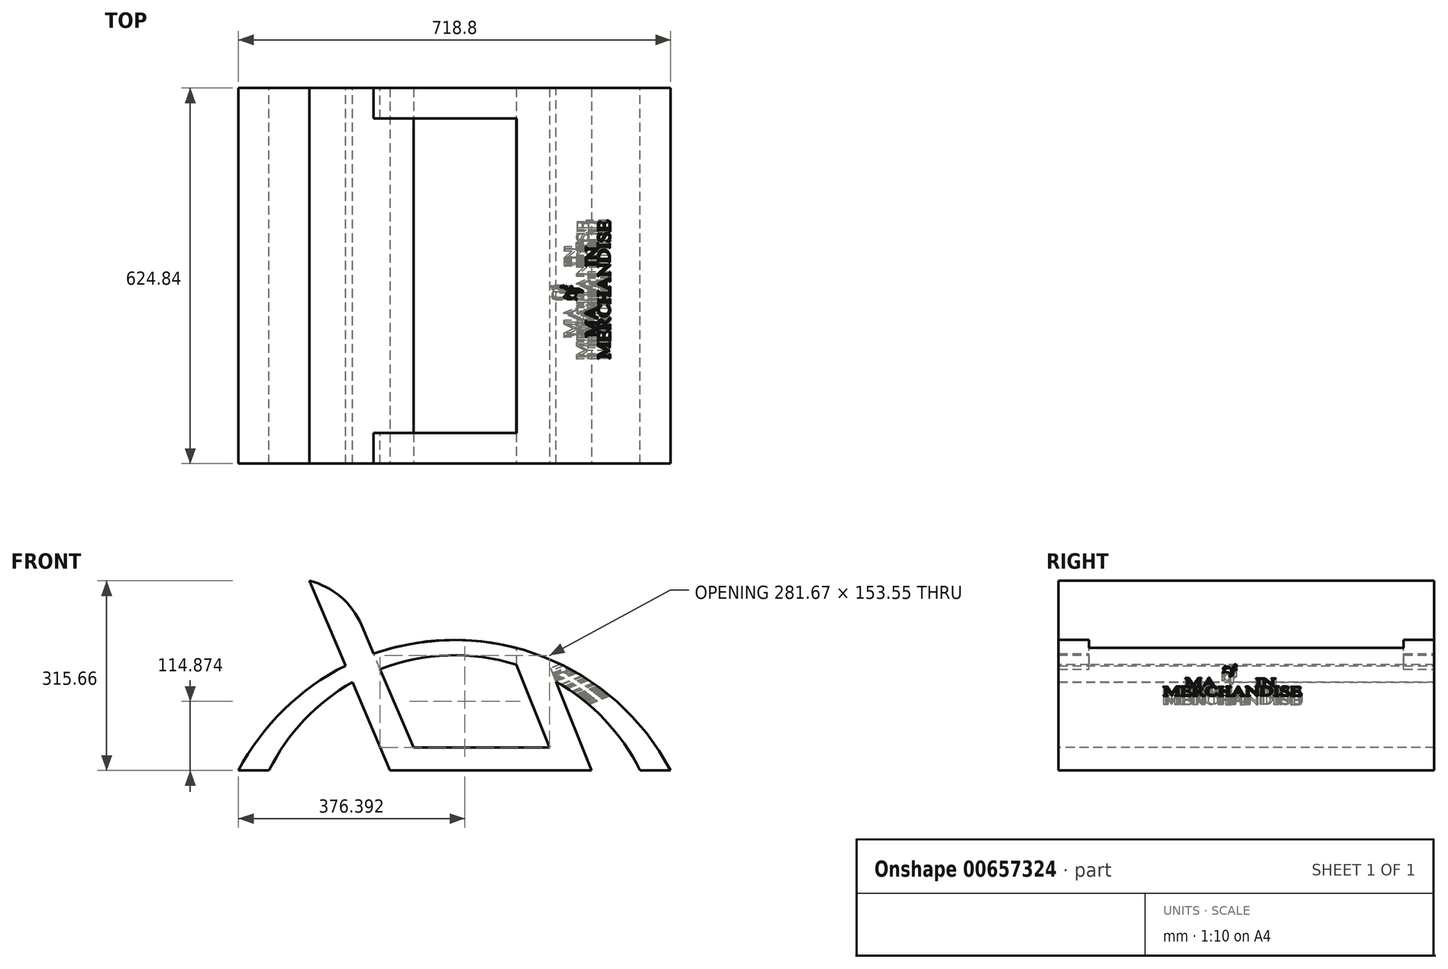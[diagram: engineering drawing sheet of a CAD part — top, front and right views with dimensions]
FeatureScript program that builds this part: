
annotation { "Feature Type Name" : "Feature", "Feature Type Description" : "" }
export const myFeature = defineFeature(function(context is Context, id is Id, definition is map)
    precondition{}
    {
        {
            var Q0;
            Q0=qCreatedBy(makeId("Front.planeOp"),FACE);
            var sketch = newSketch(context, id + "F0", { "sketchPlane" : qUnion([Q0])});
            skArc(sketch, "E0", {"start": v(359.4, -297.32) * mm, "mid": v(0, -80.1) * mm, "end": v(-359.4, -297.32) * mm});
            skArc(sketch, "E1", {"start": v(308.6, -297.32) * mm, "mid": v(0, -105.5) * mm, "end": v(-308.6, -297.32) * mm});
            skLineSegment(sketch, "E2", {"start": v(-359.4, -297.32) * mm, "end": v(-308.6, -297.32) * mm});
            skLineSegment(sketch, "E3", {"start": v(308.6, -297.32) * mm, "end": v(359.4, -297.32) * mm});
            skSolve(sketch);
        }
        {
            var Q0;
            Q0=qSketchRegion(id+"F0",true);
            extrude(context, id + "F1", {"entities" : qUnion([Q0]), "depth" : 624.84 * mm, "offsetDistance" : 25.4 * mm});
        }
        {
            var Q0;
            Q0=makeQuery(id+"F1.opExtrude","CAP_FACE",FACE,{"disambiguationData":[OSD([sQuery(id+"F0.wireOp",EDGE,"E0"),sQuery(id+"F0.wireOp",EDGE,"E1"),sQuery(id+"F0.wireOp",EDGE,"E2"),sQuery(id+"F0.wireOp",EDGE,"E3")])],"isStart":false});
            var sketch = newSketch(context, id + "F2", { "sketchPlane" : qUnion([Q0])});
            skLineSegment(sketch, "E4", {"start": v(-241.38, 18.34) * mm, "end": v(-107.4, -297.32) * mm});
            skLineSegment(sketch, "E5", {"start": v(-107.4, -297.32) * mm, "end": v(227.72, -297.32) * mm});
            skLineSegment(sketch, "E6", {"start": v(227.72, -297.32) * mm, "end": v(153.02, -110.04) * mm});
            skLineSegment(sketch, "E7", {"start": v(-68.38, -259.22) * mm, "end": v(157.83, -259.22) * mm});
            skLineSegment(sketch, "E8", {"start": v(157.83, -259.22) * mm, "end": v(102.78, -121.2) * mm});
            skLineSegment(sketch, "E9", {"start": v(102.78, -121.2) * mm, "end": v(153.02, -110.04) * mm});
            skLineSegment(sketch, "E10", {"start": v(-68.38, -259.22) * mm, "end": v(-154.8, -55.64) * mm});
            skArc(sketch, "E11", {"start": v(-154.8, -55.64) * mm, "mid": v(-189.38, -8.46) * mm, "end": v(-241.38, 18.34) * mm});
            skSolve(sketch);
        }
        {
            var Q0;
            Q0=qCreatedBy(makeId("Top.planeOp"),FACE);
            var sketch = newSketch(context, id + "F3", { "sketchPlane" : qUnion([Q0])});
            skLineSegment(sketch, "E12.bottom", {"start": v(-163.5, -50.8) * mm, "end": v(103.2, -50.8) * mm});
            skLineSegment(sketch, "E12.top", {"start": v(-163.5, -574.04) * mm, "end": v(103.2, -574.04) * mm});
            skLineSegment(sketch, "E12.left", {"start": v(-163.5, -50.8) * mm, "end": v(-163.5, -574.04) * mm});
            skLineSegment(sketch, "E12.right", {"start": v(103.2, -50.8) * mm, "end": v(103.2, -574.04) * mm});
            skSolve(sketch);
        }
        {
            var Q0;
            Q0=qSketchRegion(id+"F3",true);
            extrude(context, id + "F4", {"entities" : qUnion([Q0]), "operationType" : NewBodyOperationType.REMOVE, "oppositeDirection" : true, "depth" : 251.46 * mm, "offsetDistance" : 25.4 * mm});
        }
        {
            var Q0;
            Q0=qSketchRegion(id+"F2",true);
            extrude(context, id + "F5", {"entities" : qUnion([Q0]), "operationType" : NewBodyOperationType.ADD, "oppositeDirection" : true, "depth" : 624.84 * mm, "offsetDistance" : 25.4 * mm});
        }
        {
            var Q0;
            Q0=makeQuery(id+"F5.opExtrude","SWEPT_FACE",FACE,{"disambiguationData":[OSD([sQuery(id+"F2.wireOp",EDGE,"E6")])]});
            var sketch = newSketch(context, id + "F6", { "sketchPlane" : qUnion([Q0])});
            skFitSpline(sketch, "E13", {"points": [v(-335.35, -191.62) * mm, v(-335.44, -189.93) * mm, v(-335.7, -187.4) * mm, v(-334.92, -184.76) * mm, v(-333.7, -182.79) * mm, v(-332.39, -181.38) * mm, v(-332.12, -179.22) * mm, v(-331.95, -177.52) * mm, v(-331.08, -177.24) * mm, v(-329.94, -177.43) * mm, v(-329.77, -178.75) * mm, v(-329.42, -180.44) * mm, v(-328.2, -181.1) * mm, v(-328.54, -181.85) * mm, v(-329.42, -182.32) * mm, v(-329.77, -183.16) * mm, v(-329.77, -184.57) * mm, v(-329.85, -185.42) * mm, v(-330.99, -185.6) * mm, v(-331.95, -186.17) * mm, v(-333, -186.92) * mm, v(-333.6, -188.52) * mm, v(-333.87, -190.5) * mm, v(-333.87, -191.62) * mm, v(-332.82, -190.96) * mm, v(-331.08, -190.96) * mm, v(-329.42, -192.28) * mm, v(-329.6, -193.31) * mm, v(-331.95, -194.16) * mm, v(-333.26, -195.2) * mm, v(-333.87, -197.07) * mm, v(-333.96, -199.7) * mm], "startDerivative": vector(-0.27, 47.79) * mm, "endDerivative": vector(0.97, -64.68) * mm});
            skFitSpline(sketch, "E14", {"points": [v(-333.96, -199.7) * mm, v(-333.96, -201.04) * mm, v(-333.96, -202.6) * mm, v(-333.96, -203.72) * mm, v(-334.56, -205.07) * mm, v(-335.96, -207.75) * mm, v(-337.93, -209.6) * mm, v(-339.7, -209.76) * mm, v(-340.37, -208.92) * mm, v(-340.43, -208.42) * mm, v(-339.7, -208.48) * mm, v(-338.66, -207.8) * mm, v(-338.6, -206.58) * mm, v(-339.44, -205.51) * mm, v(-339.7, -203.56) * mm, v(-339.6, -202.5) * mm, v(-341.1, -201.2) * mm, v(-341.72, -201.15) * mm, v(-341.72, -200.15) * mm, v(-342.2, -199.2) * mm, v(-344.22, -199.25) * mm, v(-345.57, -199.09) * mm, v(-346.19, -198.2) * mm, v(-347.38, -196.8) * mm, v(-347.95, -196.9) * mm, v(-348.16, -198.14) * mm, v(-348.89, -198.97) * mm, v(-351.28, -200.15) * mm, v(-353.04, -198.92) * mm, v(-350.8, -198.7) * mm, v(-349.56, -196.8) * mm, v(-349.1, -194.5) * mm], "startDerivative": vector(0.31, -42.03) * mm, "endDerivative": vector(9.9, 54.9) * mm});
            skFitSpline(sketch, "E15", {"points": [v(-349.1, -194.5) * mm, v(-350.5, -193.44) * mm, v(-350.86, -192.66) * mm, v(-350.24, -192.1) * mm, v(-350.5, -191.43) * mm, v(-351.64, -190.42) * mm, v(-351.38, -189.98) * mm, v(-350.7, -189.42) * mm, v(-351.12, -188.41) * mm, v(-350.63, -187) * mm, v(-350.38, -186) * mm, v(-349.77, -185.53) * mm, v(-349.1, -184.2) * mm, v(-348.4, -183.34) * mm, v(-348.6, -182.14) * mm, v(-348.22, -181.81) * mm, v(-347.6, -181.61) * mm, v(-346.74, -182.28) * mm, v(-345.82, -183.47) * mm, v(-342.98, -184.54) * mm, v(-340.26, -186.4) * mm, v(-337.73, -189) * mm, v(-337.48, -189.92) * mm, v(-336.8, -190.32) * mm, v(-336.68, -190.65) * mm, v(-336.5, -191.38) * mm, v(-336.12, -192.25) * mm, v(-335.35, -191.62) * mm], "startDerivative": vector(-33.51, 22.16) * mm, "endDerivative": vector(25.24, 30.1) * mm});
            skFitSpline(sketch, "E16", {"points": [v(-349.7, -190.19) * mm, v(-349.03, -188.41) * mm, v(-347.67, -187.13) * mm, v(-347.42, -186.27) * mm, v(-346.99, -185.87) * mm, v(-346.37, -186) * mm, v(-346.06, -186.86) * mm, v(-345.75, -186) * mm, v(-344.77, -185.8) * mm, v(-343.16, -186.2) * mm, v(-341.3, -187.2) * mm, v(-340.14, -187.73) * mm, v(-339.02, -188.41) * mm, v(-338.65, -189.42) * mm, v(-338.35, -189.99) * mm, v(-338.53, -190.52) * mm, v(-339.95, -189.42) * mm, v(-341.62, -188.41) * mm, v(-343.16, -188.41) * mm, v(-344.7, -188.41) * mm, v(-345.63, -189.42) * mm, v(-346.74, -190.32) * mm, v(-347.54, -191.12) * mm, v(-348.22, -191.12) * mm, v(-349.7, -190.19) * mm]});
            skLineSegment(sketch, "E17", {"start": v(-442.75, -256.74) * mm, "end": v(-442.75, -255.25) * mm});
            skLineSegment(sketch, "E18", {"start": v(-442.75, -255.25) * mm, "end": v(-445.49, -255.25) * mm});
            skLineSegment(sketch, "E19", {"start": v(-445.49, -255.25) * mm, "end": v(-445.49, -239.64) * mm});
            skLineSegment(sketch, "E20", {"start": v(-445.49, -239.64) * mm, "end": v(-436.87, -256.58) * mm});
            skLineSegment(sketch, "E21", {"start": v(-436.87, -256.58) * mm, "end": v(-428.5, -238.13) * mm});
            skLineSegment(sketch, "E22", {"start": v(-428.5, -238.13) * mm, "end": v(-428.5, -255.16) * mm});
            skLineSegment(sketch, "E23", {"start": v(-428.5, -255.16) * mm, "end": v(-432.12, -255.16) * mm});
            skLineSegment(sketch, "E24", {"start": v(-432.12, -255.16) * mm, "end": v(-432.12, -256.33) * mm});
            skLineSegment(sketch, "E25", {"start": v(-432.12, -256.33) * mm, "end": v(-422.87, -256.33) * mm});
            skLineSegment(sketch, "E26", {"start": v(-422.87, -256.33) * mm, "end": v(-422.87, -255.25) * mm});
            skLineSegment(sketch, "E27", {"start": v(-422.87, -255.25) * mm, "end": v(-425.95, -255.25) * mm});
            skLineSegment(sketch, "E28", {"start": v(-425.95, -255.25) * mm, "end": v(-425.95, -235.85) * mm});
            skLineSegment(sketch, "E29", {"start": v(-425.95, -235.85) * mm, "end": v(-422.6, -235.85) * mm});
            skLineSegment(sketch, "E30", {"start": v(-422.6, -235.85) * mm, "end": v(-422.6, -234.76) * mm});
            skLineSegment(sketch, "E31", {"start": v(-422.6, -234.76) * mm, "end": v(-429.42, -234.76) * mm});
            skLineSegment(sketch, "E32", {"start": v(-429.42, -234.76) * mm, "end": v(-436.5, -250.52) * mm});
            skLineSegment(sketch, "E33", {"start": v(-436.5, -250.52) * mm, "end": v(-443.59, -234.98) * mm});
            skLineSegment(sketch, "E34", {"start": v(-443.59, -234.98) * mm, "end": v(-450.58, -234.98) * mm});
            skLineSegment(sketch, "E35", {"start": v(-450.58, -234.98) * mm, "end": v(-450.58, -235.98) * mm});
            skLineSegment(sketch, "E36", {"start": v(-450.58, -235.98) * mm, "end": v(-447.14, -235.98) * mm});
            skLineSegment(sketch, "E37", {"start": v(-447.14, -235.98) * mm, "end": v(-447.14, -255.15) * mm});
            skLineSegment(sketch, "E38", {"start": v(-447.14, -255.15) * mm, "end": v(-450.16, -255.15) * mm});
            skLineSegment(sketch, "E39", {"start": v(-450.16, -255.15) * mm, "end": v(-450.22, -256.74) * mm});
            skLineSegment(sketch, "E40", {"start": v(-421.53, -234.76) * mm, "end": v(-421.53, -235.85) * mm});
            skLineSegment(sketch, "E41", {"start": v(-421.53, -235.85) * mm, "end": v(-418.8, -235.85) * mm});
            skLineSegment(sketch, "E42", {"start": v(-418.8, -235.85) * mm, "end": v(-418.8, -255.15) * mm});
            skLineSegment(sketch, "E43", {"start": v(-418.8, -255.15) * mm, "end": v(-421.79, -255.15) * mm});
            skLineSegment(sketch, "E44", {"start": v(-421.79, -255.15) * mm, "end": v(-421.79, -256.69) * mm});
            skLineSegment(sketch, "E45", {"start": v(-421.79, -256.69) * mm, "end": v(-405.11, -256.69) * mm});
            skLineSegment(sketch, "E46", {"start": v(-405.11, -256.69) * mm, "end": v(-402.76, -251.15) * mm});
            skLineSegment(sketch, "E47", {"start": v(-402.76, -251.15) * mm, "end": v(-404.21, -250.53) * mm});
            skLineSegment(sketch, "E48", {"start": v(-404.21, -250.53) * mm, "end": v(-406.27, -255.4) * mm});
            skLineSegment(sketch, "E49", {"start": v(-406.27, -255.4) * mm, "end": v(-415.53, -255.4) * mm});
            skLineSegment(sketch, "E50", {"start": v(-415.53, -255.4) * mm, "end": v(-415.53, -246.5) * mm});
            skLineSegment(sketch, "E51", {"start": v(-415.53, -246.5) * mm, "end": v(-408.78, -246.5) * mm});
            skArc(sketch, "E52", {"start": v(-407.98, -249.08) * mm, "mid": v(-408.19, -247.74) * mm, "end": v(-408.78, -246.5) * mm});
            skArc(sketch, "E53", {"start": v(-408.78, -244.41) * mm, "mid": v(-408.02, -243.45) * mm, "end": v(-407.67, -242.28) * mm});
            skLineSegment(sketch, "E54", {"start": v(-407.67, -242.28) * mm, "end": v(-407.17, -242.28) * mm});
            skLineSegment(sketch, "E55", {"start": v(-407.17, -242.28) * mm, "end": v(-407.17, -249.05) * mm});
            skLineSegment(sketch, "E56", {"start": v(-407.17, -249.05) * mm, "end": v(-407.98, -249.08) * mm});
            skLineSegment(sketch, "E57", {"start": v(-415.53, -244.52) * mm, "end": v(-408.78, -244.41) * mm});
            skLineSegment(sketch, "E58", {"start": v(-415.53, -244.52) * mm, "end": v(-415.66, -236.48) * mm});
            skLineSegment(sketch, "E59", {"start": v(-415.66, -236.48) * mm, "end": v(-407.47, -236.48) * mm});
            skArc(sketch, "E60", {"start": v(-406.33, -239.98) * mm, "mid": v(-406.3, -238.04) * mm, "end": v(-407.47, -236.48) * mm});
            skLineSegment(sketch, "E61", {"start": v(-406.33, -239.98) * mm, "end": v(-405.19, -239.98) * mm});
            skLineSegment(sketch, "E62", {"start": v(-405.19, -239.98) * mm, "end": v(-405.19, -234.83) * mm});
            skLineSegment(sketch, "E63", {"start": v(-405.19, -234.83) * mm, "end": v(-421.53, -234.76) * mm});
            skLineSegment(sketch, "E64", {"start": v(-238.9, -235.08) * mm, "end": v(-238.9, -236.18) * mm});
            skLineSegment(sketch, "E65", {"start": v(-238.9, -236.18) * mm, "end": v(-236.17, -236.18) * mm});
            skLineSegment(sketch, "E66", {"start": v(-236.17, -236.18) * mm, "end": v(-236.19, -255.48) * mm});
            skLineSegment(sketch, "E67", {"start": v(-236.19, -255.48) * mm, "end": v(-239.16, -255.48) * mm});
            skLineSegment(sketch, "E68", {"start": v(-239.16, -255.48) * mm, "end": v(-239.16, -257.01) * mm});
            skLineSegment(sketch, "E69", {"start": v(-239.16, -257.01) * mm, "end": v(-222.2, -257.02) * mm});
            skLineSegment(sketch, "E70", {"start": v(-222.2, -257.02) * mm, "end": v(-220.14, -251.49) * mm});
            skLineSegment(sketch, "E71", {"start": v(-220.14, -251.49) * mm, "end": v(-221.83, -250.85) * mm});
            skLineSegment(sketch, "E72", {"start": v(-221.83, -250.85) * mm, "end": v(-223.1, -254.27) * mm});
            skArc(sketch, "E73", {"start": v(-224.85, -255.85) * mm, "mid": v(-223.79, -255.27) * mm, "end": v(-223.1, -254.27) * mm});
            skLineSegment(sketch, "E74", {"start": v(-224.85, -255.85) * mm, "end": v(-232.91, -255.84) * mm});
            skLineSegment(sketch, "E75", {"start": v(-232.91, -255.84) * mm, "end": v(-232.9, -246.84) * mm});
            skLineSegment(sketch, "E76", {"start": v(-232.9, -246.84) * mm, "end": v(-226.15, -246.84) * mm});
            skArc(sketch, "E77", {"start": v(-225.35, -249.42) * mm, "mid": v(-225.56, -248.07) * mm, "end": v(-226.15, -246.84) * mm});
            skArc(sketch, "E78", {"start": v(-226.15, -244.75) * mm, "mid": v(-225.4, -243.79) * mm, "end": v(-225.04, -242.62) * mm});
            skLineSegment(sketch, "E79", {"start": v(-225.04, -242.62) * mm, "end": v(-224.54, -242.62) * mm});
            skLineSegment(sketch, "E80", {"start": v(-224.54, -242.62) * mm, "end": v(-224.54, -249.38) * mm});
            skLineSegment(sketch, "E81", {"start": v(-224.54, -249.38) * mm, "end": v(-225.35, -249.42) * mm});
            skLineSegment(sketch, "E82", {"start": v(-232.9, -244.85) * mm, "end": v(-226.15, -244.75) * mm});
            skLineSegment(sketch, "E83", {"start": v(-232.9, -244.85) * mm, "end": v(-233.02, -236.8) * mm});
            skLineSegment(sketch, "E84", {"start": v(-233.02, -236.8) * mm, "end": v(-224.84, -236.81) * mm});
            skArc(sketch, "E85", {"start": v(-223.7, -240.32) * mm, "mid": v(-223.67, -238.37) * mm, "end": v(-224.84, -236.81) * mm});
            skLineSegment(sketch, "E86", {"start": v(-223.7, -240.32) * mm, "end": v(-222.56, -240.32) * mm});
            skLineSegment(sketch, "E87", {"start": v(-222.56, -240.32) * mm, "end": v(-222.55, -235.16) * mm});
            skLineSegment(sketch, "E88", {"start": v(-222.55, -235.16) * mm, "end": v(-238.9, -235.08) * mm});
            skLineSegment(sketch, "E89.0", {"start": v(-232.9, -246.84) * mm, "end": v(-232.9, -244.85) * mm, "construction": true});
            skLineSegment(sketch, "E90.0", {"start": v(-226.15, -246.84) * mm, "end": v(-226.15, -244.75) * mm, "construction": true});
            skLineSegment(sketch, "E91", {"start": v(-399.46, -255.4) * mm, "end": v(-399.46, -236.97) * mm});
            skLineSegment(sketch, "E92", {"start": v(-399.46, -236.97) * mm, "end": v(-402.49, -235.68) * mm});
            skLineSegment(sketch, "E93", {"start": v(-402.49, -235.68) * mm, "end": v(-402.5, -234.44) * mm});
            skLineSegment(sketch, "E94", {"start": v(-402.5, -234.44) * mm, "end": v(-391.04, -234.44) * mm});
            skArc(sketch, "E95", {"start": v(-391.04, -245.74) * mm, "mid": v(-385.39, -240.09) * mm, "end": v(-391.04, -234.44) * mm});
            skArc(sketch, "E96", {"start": v(-395.75, -244.84) * mm, "mid": v(-389.61, -240.3) * mm, "end": v(-396.09, -236.25) * mm});
            skLineSegment(sketch, "E97", {"start": v(-396.09, -236.25) * mm, "end": v(-395.75, -244.84) * mm});
            skLineSegment(sketch, "E98", {"start": v(-395.75, -246.71) * mm, "end": v(-395.75, -255.4) * mm});
            skLineSegment(sketch, "E99", {"start": v(-395.75, -255.4) * mm, "end": v(-392.97, -255.4) * mm});
            skLineSegment(sketch, "E100", {"start": v(-392.97, -255.4) * mm, "end": v(-392.97, -256.66) * mm});
            skLineSegment(sketch, "E101", {"start": v(-392.97, -256.66) * mm, "end": v(-402.31, -256.66) * mm});
            skLineSegment(sketch, "E102", {"start": v(-402.31, -256.66) * mm, "end": v(-402.31, -255.4) * mm});
            skLineSegment(sketch, "E103", {"start": v(-402.31, -255.4) * mm, "end": v(-399.46, -255.4) * mm});
            skLineSegment(sketch, "E104", {"start": v(-395.75, -246.71) * mm, "end": v(-393.76, -246.71) * mm});
            skLineSegment(sketch, "E105", {"start": v(-393.76, -246.71) * mm, "end": v(-386.57, -256.7) * mm});
            skLineSegment(sketch, "E106", {"start": v(-386.57, -256.7) * mm, "end": v(-381.36, -256.7) * mm});
            skLineSegment(sketch, "E107", {"start": v(-381.36, -256.7) * mm, "end": v(-381.36, -255.4) * mm});
            skLineSegment(sketch, "E108", {"start": v(-381.36, -255.4) * mm, "end": v(-384.07, -255.4) * mm});
            skLineSegment(sketch, "E109", {"start": v(-384.07, -255.4) * mm, "end": v(-391.04, -245.74) * mm});
            skLineSegment(sketch, "E110", {"start": v(-362.13, -234.46) * mm, "end": v(-362.13, -241.27) * mm});
            skLineSegment(sketch, "E111", {"start": v(-363.87, -236.24) * mm, "end": v(-362.13, -234.46) * mm});
            skArc(sketch, "E112", {"start": v(-363.87, -236.24) * mm, "mid": v(-380.25, -244.3) * mm, "end": v(-366.7, -256.56) * mm});
            skFitSpline(sketch, "E113", {"points": [v(-362.13, -241.27) * mm, v(-364.55, -237.77) * mm, v(-368.44, -236.32) * mm, v(-372.72, -237.44) * mm, v(-375.26, -241.59) * mm], "startDerivative": vector(-8.42, 15.94) * mm, "endDerivative": vector(-7.7, -18.3) * mm});
            skFitSpline(sketch, "E114", {"points": [v(-375.26, -241.59) * mm, v(-375.68, -249.47) * mm, v(-373.4, -253.08) * mm, v(-370.42, -254.51) * mm, v(-367.3, -254.85) * mm, v(-364.88, -253.73) * mm, v(-362.13, -250.86) * mm, v(-361.3, -250.74) * mm, v(-361.06, -251.65) * mm, v(-362.13, -253.6) * mm, v(-363.84, -255.43) * mm, v(-366.7, -256.56) * mm], "startDerivative": vector(-9.26, -57.49) * mm, "endDerivative": vector(-33.48, -9.75) * mm});
            skArc(sketch, "E115", {"start": v(-284.23, -254.17) * mm, "mid": v(-272.32, -245.7) * mm, "end": v(-284.2, -237.18) * mm});
            skArc(sketch, "E116", {"start": v(-278.73, -255.89) * mm, "mid": v(-268.91, -245.3) * mm, "end": v(-278.5, -234.52) * mm});
            skLineSegment(sketch, "E117", {"start": v(-278.73, -255.89) * mm, "end": v(-289.78, -255.89) * mm});
            skLineSegment(sketch, "E118", {"start": v(-289.78, -255.89) * mm, "end": v(-289.78, -254.4) * mm});
            skLineSegment(sketch, "E119", {"start": v(-289.78, -254.4) * mm, "end": v(-287.8, -254.4) * mm});
            skLineSegment(sketch, "E120", {"start": v(-287.8, -254.4) * mm, "end": v(-287.3, -235.76) * mm});
            skLineSegment(sketch, "E121", {"start": v(-287.3, -235.76) * mm, "end": v(-290.05, -235.7) * mm});
            skLineSegment(sketch, "E122", {"start": v(-290.05, -235.7) * mm, "end": v(-290.05, -234.57) * mm});
            skLineSegment(sketch, "E123", {"start": v(-290.05, -234.57) * mm, "end": v(-278.5, -234.52) * mm});
            skLineSegment(sketch, "E124", {"start": v(-353.22, -244.38) * mm, "end": v(-343.8, -244.38) * mm});
            skLineSegment(sketch, "E125", {"start": v(-353.42, -254.95) * mm, "end": v(-353.42, -246.74) * mm});
            skLineSegment(sketch, "E126", {"start": v(-353.42, -246.74) * mm, "end": v(-343.93, -246.74) * mm});
            skFitSpline(sketch, "E127", {"points": [v(-353.42, -254.95) * mm, v(-353.15, -255.5) * mm, v(-352.52, -255.63) * mm], "startDerivative": vector(0.37, -1.35) * mm, "endDerivative": vector(1.42, 0.17) * mm});
            skLineSegment(sketch, "E128", {"start": v(-352.52, -255.63) * mm, "end": v(-350.68, -255.63) * mm});
            skLineSegment(sketch, "E129", {"start": v(-350.68, -255.63) * mm, "end": v(-350.68, -256.68) * mm});
            skLineSegment(sketch, "E130", {"start": v(-350.68, -256.68) * mm, "end": v(-358.19, -256.68) * mm});
            skLineSegment(sketch, "E131", {"start": v(-358.19, -256.68) * mm, "end": v(-359.36, -256.68) * mm});
            skLineSegment(sketch, "E132", {"start": v(-359.36, -256.68) * mm, "end": v(-359.36, -255.63) * mm});
            skLineSegment(sketch, "E133", {"start": v(-359.36, -255.63) * mm, "end": v(-357.47, -255.63) * mm});
            skLineSegment(sketch, "E134", {"start": v(-356.6, -255.3) * mm, "end": v(-356.6, -237.36) * mm});
            skFitSpline(sketch, "E135", {"points": [v(-356.6, -237.36) * mm, v(-356.9, -236.25) * mm, v(-358.24, -236.05) * mm], "startDerivative": vector(-0.68, 2.41) * mm, "endDerivative": vector(-2.6, 0.22) * mm});
            skLineSegment(sketch, "E136", {"start": v(-358.24, -236.05) * mm, "end": v(-359.43, -236.05) * mm});
            skLineSegment(sketch, "E137", {"start": v(-359.43, -236.05) * mm, "end": v(-359.43, -235.16) * mm});
            skLineSegment(sketch, "E138", {"start": v(-359.43, -235.16) * mm, "end": v(-350.57, -235.16) * mm});
            skLineSegment(sketch, "E139", {"start": v(-350.57, -235.16) * mm, "end": v(-350.57, -236.05) * mm});
            skLineSegment(sketch, "E140", {"start": v(-353.22, -244.38) * mm, "end": v(-353.22, -237.04) * mm});
            skFitSpline(sketch, "E141", {"points": [v(-353.22, -237.04) * mm, v(-353.1, -236.33) * mm, v(-352.32, -236.12) * mm, v(-350.57, -236.05) * mm], "startDerivative": vector(-0.04, 3) * mm, "endDerivative": vector(4.3, 0.15) * mm});
            skFitSpline(sketch, "E142", {"points": [v(-350.55, -236.03) * mm, v(-350.57, -236.02) * mm], "startDerivative": vector(-0.01, 0.01) * mm, "endDerivative": vector(-0.01, 0.01) * mm});
            skLineSegment(sketch, "E143", {"start": v(-284.23, -254.17) * mm, "end": v(-284.2, -237.18) * mm});
            skLineSegment(sketch, "E144", {"start": v(-267.04, -234.4) * mm, "end": v(-257.34, -234.4) * mm});
            skLineSegment(sketch, "E145", {"start": v(-257.34, -234.4) * mm, "end": v(-257.34, -235.74) * mm});
            skLineSegment(sketch, "E146", {"start": v(-257.34, -235.74) * mm, "end": v(-259.85, -235.74) * mm});
            skFitSpline(sketch, "E147", {"points": [v(-261.19, -237.54) * mm, v(-261.02, -236.68) * mm, v(-260.49, -236.04) * mm, v(-259.85, -235.74) * mm], "startDerivative": vector(0.2, 2.55) * mm, "endDerivative": vector(2.11, 0.73) * mm});
            skLineSegment(sketch, "E148", {"start": v(-261.19, -237.54) * mm, "end": v(-261.19, -253.88) * mm});
            skFitSpline(sketch, "E149", {"points": [v(-261.19, -253.88) * mm, v(-260.88, -254.79) * mm, v(-260.52, -255.24) * mm, v(-259.84, -255.26) * mm], "startDerivative": vector(0.77, -2.51) * mm, "endDerivative": vector(2.36, 0.38) * mm});
            skLineSegment(sketch, "E150", {"start": v(-259.84, -255.26) * mm, "end": v(-258.16, -255.26) * mm});
            skLineSegment(sketch, "E151", {"start": v(-258.16, -255.26) * mm, "end": v(-258.16, -256.42) * mm});
            skLineSegment(sketch, "E152", {"start": v(-258.16, -256.42) * mm, "end": v(-266.64, -256.42) * mm});
            skLineSegment(sketch, "E153", {"start": v(-266.64, -256.42) * mm, "end": v(-266.64, -255.24) * mm});
            skFitSpline(sketch, "E154", {"points": [v(-266.64, -255.24) * mm, v(-264.58, -255.24) * mm, v(-263.91, -253.62) * mm], "startDerivative": vector(2.9, -0.56) * mm, "endDerivative": vector(0.76, 2.78) * mm});
            skLineSegment(sketch, "E155", {"start": v(-267.04, -234.4) * mm, "end": v(-267.04, -236.03) * mm});
            skFitSpline(sketch, "E156", {"points": [v(-267.04, -236.03) * mm, v(-264.62, -236.03) * mm, v(-263.91, -237.31) * mm], "startDerivative": vector(4.2, 0.09) * mm, "endDerivative": vector(-0.03, -6.33) * mm});
            skLineSegment(sketch, "E157", {"start": v(-263.91, -237.31) * mm, "end": v(-263.91, -253.62) * mm});
            skLineSegment(sketch, "E158", {"start": v(-329.38, -247.56) * mm, "end": v(-326.39, -239.8) * mm});
            skLineSegment(sketch, "E159", {"start": v(-326.39, -239.8) * mm, "end": v(-323.06, -247.74) * mm});
            skLineSegment(sketch, "E160", {"start": v(-323.06, -247.74) * mm, "end": v(-329.38, -247.56) * mm});
            skLineSegment(sketch, "E161", {"start": v(-332.84, -255.44) * mm, "end": v(-330.66, -249.6) * mm});
            skLineSegment(sketch, "E162", {"start": v(-330.66, -249.6) * mm, "end": v(-322.33, -249.6) * mm});
            skLineSegment(sketch, "E163", {"start": v(-322.33, -249.6) * mm, "end": v(-320.16, -255.43) * mm});
            skLineSegment(sketch, "E164", {"start": v(-336.48, -256.64) * mm, "end": v(-330.32, -256.64) * mm});
            skLineSegment(sketch, "E165", {"start": v(-322.7, -256.82) * mm, "end": v(-314.7, -256.82) * mm});
            skLineSegment(sketch, "E166", {"start": v(-314.7, -256.82) * mm, "end": v(-314.7, -255.43) * mm});
            skLineSegment(sketch, "E167", {"start": v(-335.07, -255.43) * mm, "end": v(-326.63, -234.81) * mm});
            skLineSegment(sketch, "E168", {"start": v(-326.63, -234.81) * mm, "end": v(-325.16, -234.81) * mm});
            skLineSegment(sketch, "E169", {"start": v(-325.16, -234.81) * mm, "end": v(-316.57, -255.43) * mm});
            skLineSegment(sketch, "E170", {"start": v(-316.57, -255.43) * mm, "end": v(-314.7, -255.43) * mm});
            skLineSegment(sketch, "E171", {"start": v(-336.48, -255.43) * mm, "end": v(-335.07, -255.43) * mm});
            skLineSegment(sketch, "E172", {"start": v(-336.48, -256.64) * mm, "end": v(-336.48, -255.43) * mm});
            skLineSegment(sketch, "E173", {"start": v(-332.84, -255.44) * mm, "end": v(-330.32, -255.44) * mm});
            skLineSegment(sketch, "E174", {"start": v(-330.32, -255.44) * mm, "end": v(-330.32, -256.64) * mm});
            skLineSegment(sketch, "E175", {"start": v(-322.7, -255.43) * mm, "end": v(-320.16, -255.43) * mm});
            skLineSegment(sketch, "E176", {"start": v(-322.7, -255.43) * mm, "end": v(-322.7, -256.82) * mm});
            skLineSegment(sketch, "E177", {"start": v(-450.22, -256.74) * mm, "end": v(-442.75, -256.74) * mm});
            skLineSegment(sketch, "E178", {"start": v(-298.15, -234.57) * mm, "end": v(-291.53, -234.57) * mm});
            skLineSegment(sketch, "E179", {"start": v(-291.53, -234.57) * mm, "end": v(-291.53, -235.88) * mm});
            skLineSegment(sketch, "E180", {"start": v(-291.53, -235.88) * mm, "end": v(-293.87, -235.88) * mm});
            skLineSegment(sketch, "E181", {"start": v(-293.87, -235.88) * mm, "end": v(-293.87, -256.81) * mm});
            skLineSegment(sketch, "E182", {"start": v(-293.87, -256.81) * mm, "end": v(-295.3, -256.81) * mm});
            skLineSegment(sketch, "E183", {"start": v(-295.3, -256.81) * mm, "end": v(-308.9, -239.62) * mm});
            skLineSegment(sketch, "E184", {"start": v(-308.9, -239.62) * mm, "end": v(-308.9, -255.59) * mm});
            skLineSegment(sketch, "E185", {"start": v(-308.9, -255.59) * mm, "end": v(-306.2, -255.59) * mm});
            skLineSegment(sketch, "E186", {"start": v(-306.2, -255.59) * mm, "end": v(-306.2, -256.65) * mm});
            skLineSegment(sketch, "E187", {"start": v(-306.2, -256.65) * mm, "end": v(-313.25, -256.65) * mm});
            skLineSegment(sketch, "E188", {"start": v(-313.25, -256.65) * mm, "end": v(-313.25, -255.55) * mm});
            skLineSegment(sketch, "E189", {"start": v(-313.25, -255.55) * mm, "end": v(-310.58, -255.55) * mm});
            skLineSegment(sketch, "E190", {"start": v(-310.58, -255.55) * mm, "end": v(-310.58, -236.8) * mm});
            skLineSegment(sketch, "E191", {"start": v(-310.58, -236.8) * mm, "end": v(-310.95, -236.37) * mm});
            skLineSegment(sketch, "E192", {"start": v(-310.95, -236.37) * mm, "end": v(-313.78, -236.37) * mm});
            skLineSegment(sketch, "E193", {"start": v(-313.78, -236.37) * mm, "end": v(-313.78, -234.73) * mm});
            skLineSegment(sketch, "E194", {"start": v(-313.78, -234.73) * mm, "end": v(-308.9, -234.73) * mm});
            skLineSegment(sketch, "E195", {"start": v(-308.9, -234.73) * mm, "end": v(-295.75, -250.35) * mm});
            skLineSegment(sketch, "E196", {"start": v(-295.75, -250.35) * mm, "end": v(-295.75, -235.76) * mm});
            skLineSegment(sketch, "E197", {"start": v(-295.75, -235.76) * mm, "end": v(-298.15, -235.76) * mm});
            skLineSegment(sketch, "E198", {"start": v(-298.15, -235.76) * mm, "end": v(-298.15, -234.57) * mm});
            skLineSegment(sketch, "E199", {"start": v(-242.58, -242.07) * mm, "end": v(-242.58, -234.65) * mm});
            skLineSegment(sketch, "E200", {"start": v(-242.58, -234.65) * mm, "end": v(-243.18, -234.65) * mm});
            skLineSegment(sketch, "E201", {"start": v(-242.58, -242.07) * mm, "end": v(-243.38, -242.07) * mm});
            skFitSpline(sketch, "E202", {"points": [v(-243.18, -234.65) * mm, v(-243.18, -235.64) * mm, v(-244.29, -235.67) * mm, v(-245.9, -234.65) * mm, v(-250.62, -234.65) * mm, v(-253.65, -236.3) * mm, v(-254.9, -240.06) * mm, v(-254.62, -242.7) * mm, v(-252.08, -245.1) * mm, v(-245, -249.34) * mm, v(-243.9, -252.12) * mm, v(-245.1, -254.46) * mm, v(-248.44, -255.2) * mm, v(-251.34, -254.31) * mm, v(-253.58, -252.04) * mm, v(-253.95, -249.5) * mm], "startDerivative": vector(8.48, -32.81) * mm, "endDerivative": vector(0.27, 42.67) * mm});
            skFitSpline(sketch, "E203", {"points": [v(-243.38, -242.07) * mm, v(-243.94, -238.78) * mm, v(-246.46, -237.04) * mm, v(-250.42, -236.9) * mm, v(-252.27, -237.92) * mm, v(-252.2, -240.31) * mm, v(-250.75, -242.07) * mm, v(-246.4, -244.5) * mm, v(-241.75, -248.19) * mm, v(-241.33, -253.38) * mm, v(-245, -256.66) * mm, v(-250.1, -256.98) * mm, v(-252.28, -255.8) * mm, v(-253.3, -255.32) * mm, v(-253.95, -255.56) * mm, v(-254.03, -256.53) * mm], "startDerivative": vector(-1.08, 51.46) * mm, "endDerivative": vector(3.1, -29.81) * mm});
            skLineSegment(sketch, "E204", {"start": v(-254.03, -256.53) * mm, "end": v(-254.03, -257.05) * mm});
            skLineSegment(sketch, "E205", {"start": v(-254.03, -257.05) * mm, "end": v(-255.15, -257.05) * mm});
            skLineSegment(sketch, "E206", {"start": v(-255.15, -257.05) * mm, "end": v(-255.15, -249.44) * mm});
            skLineSegment(sketch, "E207", {"start": v(-255.15, -249.44) * mm, "end": v(-253.95, -249.5) * mm});
            skFitSpline(sketch, "E208", {"points": [v(-357.47, -255.63) * mm, v(-357.21, -255.63) * mm, v(-356.91, -255.56) * mm, v(-356.73, -255.48) * mm, v(-356.6, -255.3) * mm], "startDerivative": vector(0.97, -0.06) * mm, "endDerivative": vector(0.5, 0.87) * mm});
            skLineSegment(sketch, "E209", {"start": v(-343.93, -246.74) * mm, "end": v(-343.93, -254.57) * mm});
            skLineSegment(sketch, "E210", {"start": v(-340.93, -254.57) * mm, "end": v(-340.93, -237.37) * mm});
            skLineSegment(sketch, "E211", {"start": v(-343.66, -237.24) * mm, "end": v(-343.8, -244.38) * mm});
            skLineSegment(sketch, "E212", {"start": v(-347.04, -255.43) * mm, "end": v(-347.04, -256.9) * mm});
            skLineSegment(sketch, "E213", {"start": v(-347.04, -256.9) * mm, "end": v(-337.23, -256.9) * mm});
            skLineSegment(sketch, "E214", {"start": v(-337.23, -256.9) * mm, "end": v(-337.23, -255.76) * mm});
            skLineSegment(sketch, "E215", {"start": v(-337.23, -255.76) * mm, "end": v(-339.47, -255.76) * mm});
            skFitSpline(sketch, "E216", {"points": [v(-347.04, -255.43) * mm, v(-345.67, -255.43) * mm, v(-344.3, -255.43) * mm, v(-343.93, -254.57) * mm], "startDerivative": vector(4.85, -0.05) * mm, "endDerivative": vector(0.33, 4.53) * mm});
            skFitSpline(sketch, "E217", {"points": [v(-340.93, -254.57) * mm, v(-340.93, -255.43) * mm, v(-339.47, -255.76) * mm], "startDerivative": vector(0.14, -1.71) * mm, "endDerivative": vector(4.5, 0.27) * mm});
            skLineSegment(sketch, "E218", {"start": v(-347.16, -235.87) * mm, "end": v(-347.16, -234.74) * mm});
            skLineSegment(sketch, "E219", {"start": v(-347.16, -234.74) * mm, "end": v(-337.15, -234.74) * mm});
            skLineSegment(sketch, "E220", {"start": v(-337.15, -234.74) * mm, "end": v(-337.15, -235.92) * mm});
            skLineSegment(sketch, "E221", {"start": v(-337.15, -235.92) * mm, "end": v(-339.38, -235.92) * mm});
            skLineSegment(sketch, "E222", {"start": v(-347.16, -235.87) * mm, "end": v(-344.48, -235.87) * mm});
            skFitSpline(sketch, "E223", {"points": [v(-344.48, -235.87) * mm, v(-343.66, -237.24) * mm], "startDerivative": vector(2.58, -0.16) * mm, "endDerivative": vector(-0.12, -2.08) * mm});
            skFitSpline(sketch, "E224", {"points": [v(-340.93, -237.37) * mm, v(-339.38, -235.92) * mm], "startDerivative": vector(-0.12, 2.88) * mm, "endDerivative": vector(4.42, -0.05) * mm});
            skLineSegment(sketch, "E225", {"start": v(-409.6, -233.52) * mm, "end": v(-409.6, -218.43) * mm});
            skLineSegment(sketch, "E226", {"start": v(-392.87, -218.65) * mm, "end": v(-392.87, -233.52) * mm});
            skLineSegment(sketch, "E227", {"start": v(-389.56, -233.59) * mm, "end": v(-389.56, -215.24) * mm});
            skLineSegment(sketch, "E228", {"start": v(-389.56, -215.24) * mm, "end": v(-386.67, -215.24) * mm});
            skLineSegment(sketch, "E229", {"start": v(-386.67, -215.24) * mm, "end": v(-386.67, -214.13) * mm});
            skLineSegment(sketch, "E230", {"start": v(-386.67, -214.13) * mm, "end": v(-392.81, -214.13) * mm});
            skLineSegment(sketch, "E231", {"start": v(-392.81, -214.13) * mm, "end": v(-400.4, -229.96) * mm});
            skLineSegment(sketch, "E232", {"start": v(-400.4, -229.96) * mm, "end": v(-407.75, -214.13) * mm});
            skLineSegment(sketch, "E233", {"start": v(-407.75, -214.13) * mm, "end": v(-414.54, -214.13) * mm});
            skLineSegment(sketch, "E234", {"start": v(-414.54, -214.13) * mm, "end": v(-414.54, -215.59) * mm});
            skLineSegment(sketch, "E235", {"start": v(-414.54, -215.59) * mm, "end": v(-411.24, -215.59) * mm});
            skLineSegment(sketch, "E236", {"start": v(-411.24, -215.59) * mm, "end": v(-411.24, -233.52) * mm});
            skLineSegment(sketch, "E237", {"start": v(-411.24, -233.52) * mm, "end": v(-409.6, -233.52) * mm});
            skLineSegment(sketch, "E238", {"start": v(-409.6, -218.43) * mm, "end": v(-402.5, -233.52) * mm});
            skLineSegment(sketch, "E239", {"start": v(-402.5, -233.52) * mm, "end": v(-399.75, -233.52) * mm});
            skLineSegment(sketch, "E240", {"start": v(-399.75, -233.52) * mm, "end": v(-392.87, -218.65) * mm});
            skLineSegment(sketch, "E241", {"start": v(-378.17, -226.06) * mm, "end": v(-375.17, -218.3) * mm});
            skLineSegment(sketch, "E242", {"start": v(-375.17, -218.3) * mm, "end": v(-371.85, -226.24) * mm});
            skLineSegment(sketch, "E243", {"start": v(-371.85, -226.24) * mm, "end": v(-378.17, -226.06) * mm});
            skLineSegment(sketch, "E244", {"start": v(-381.62, -233.94) * mm, "end": v(-379.45, -228.1) * mm});
            skLineSegment(sketch, "E245", {"start": v(-379.45, -228.1) * mm, "end": v(-371.1, -228.1) * mm});
            skLineSegment(sketch, "E246", {"start": v(-371.1, -228.1) * mm, "end": v(-368.95, -233.93) * mm});
            skLineSegment(sketch, "E247", {"start": v(-383.86, -233.93) * mm, "end": v(-375.42, -213.31) * mm});
            skLineSegment(sketch, "E248", {"start": v(-375.42, -213.31) * mm, "end": v(-373.95, -213.31) * mm});
            skLineSegment(sketch, "E249", {"start": v(-373.95, -213.31) * mm, "end": v(-365.35, -233.93) * mm});
            skLineSegment(sketch, "E250", {"start": v(-383.86, -233.93) * mm, "end": v(-381.62, -233.94) * mm});
            skLineSegment(sketch, "E251", {"start": v(-368.95, -233.93) * mm, "end": v(-365.35, -233.93) * mm});
            skLineSegment(sketch, "E252", {"start": v(-392.87, -233.52) * mm, "end": v(-389.56, -233.59) * mm});
            skLineSegment(sketch, "E253", {"start": v(-296.66, -214.36) * mm, "end": v(-287.49, -214.36) * mm});
            skLineSegment(sketch, "E254", {"start": v(-287.49, -214.36) * mm, "end": v(-287.49, -215.32) * mm});
            skLineSegment(sketch, "E255", {"start": v(-287.49, -215.32) * mm, "end": v(-289.47, -215.32) * mm});
            skFitSpline(sketch, "E256", {"points": [v(-290.82, -216.9) * mm, v(-290.65, -216.16) * mm, v(-290.11, -215.52) * mm, v(-289.47, -215.32) * mm], "startDerivative": vector(0.2, 2.55) * mm, "endDerivative": vector(2.11, 0.73) * mm});
            skLineSegment(sketch, "E257", {"start": v(-290.82, -216.9) * mm, "end": v(-290.82, -233.24) * mm});
            skLineSegment(sketch, "E258", {"start": v(-296.66, -214.36) * mm, "end": v(-296.66, -215.51) * mm});
            skFitSpline(sketch, "E259", {"points": [v(-296.66, -215.51) * mm, v(-294.25, -215.51) * mm, v(-293.87, -216.8) * mm], "startDerivative": vector(4.2, 0.09) * mm, "endDerivative": vector(-0.03, -6.33) * mm});
            skLineSegment(sketch, "E260", {"start": v(-293.87, -216.8) * mm, "end": v(-293.87, -233.24) * mm});
            skLineSegment(sketch, "E261", {"start": v(-293.87, -233.24) * mm, "end": v(-290.82, -233.24) * mm});
            skLineSegment(sketch, "E262", {"start": v(-271.56, -214.45) * mm, "end": v(-263.8, -214.45) * mm});
            skLineSegment(sketch, "E263", {"start": v(-263.8, -214.45) * mm, "end": v(-263.8, -215.47) * mm});
            skLineSegment(sketch, "E264", {"start": v(-263.8, -215.47) * mm, "end": v(-267.24, -215.47) * mm});
            skLineSegment(sketch, "E265", {"start": v(-267.24, -215.47) * mm, "end": v(-267.24, -233.68) * mm});
            skLineSegment(sketch, "E266", {"start": v(-267.24, -233.68) * mm, "end": v(-269.85, -233.68) * mm});
            skLineSegment(sketch, "E267", {"start": v(-281.2, -219.44) * mm, "end": v(-281.2, -233.5) * mm});
            skLineSegment(sketch, "E268", {"start": v(-283.25, -217.02) * mm, "end": v(-284.64, -215.36) * mm});
            skLineSegment(sketch, "E269", {"start": v(-284.64, -215.36) * mm, "end": v(-286.67, -215.36) * mm});
            skLineSegment(sketch, "E270", {"start": v(-286.67, -215.36) * mm, "end": v(-286.67, -214.38) * mm});
            skLineSegment(sketch, "E271", {"start": v(-286.67, -214.38) * mm, "end": v(-282.04, -214.38) * mm});
            skLineSegment(sketch, "E272", {"start": v(-282.04, -214.38) * mm, "end": v(-268.67, -229.55) * mm});
            skLineSegment(sketch, "E273", {"start": v(-268.67, -229.55) * mm, "end": v(-268.67, -215.49) * mm});
            skLineSegment(sketch, "E274", {"start": v(-268.67, -215.49) * mm, "end": v(-271.56, -215.49) * mm});
            skLineSegment(sketch, "E275", {"start": v(-271.56, -215.49) * mm, "end": v(-271.56, -214.45) * mm});
            skLineSegment(sketch, "E276", {"start": v(-281.2, -219.44) * mm, "end": v(-269.85, -233.68) * mm});
            skLineSegment(sketch, "E277", {"start": v(-281.2, -233.5) * mm, "end": v(-283.25, -233.5) * mm});
            skLineSegment(sketch, "E278", {"start": v(-283.25, -233.5) * mm, "end": v(-283.25, -217.02) * mm});
            skSolve(sketch);
        }
        {
            var Q0;
            Q0 = qSketchRegion(id + "F6", true);
            extrude(context, id + "F7", {"entities" : qUnion([Q0]), "operationType" : NewBodyOperationType.REMOVE, "depth" : 111.76 * mm, "offsetDistance" : 25.4 * mm});
        }
        {
            var Q0;
            Q0=makeQuery(id+"F5.boolean.opBoolean","MERGE",FACE,{"derivedFrom":[makeQuery(id+"F1.opExtrude","CAP_FACE",FACE,{"disambiguationData":[OSD([sQuery(id+"F0.wireOp",EDGE,"E0"),sQuery(id+"F0.wireOp",EDGE,"E1"),sQuery(id+"F0.wireOp",EDGE,"E2"),sQuery(id+"F0.wireOp",EDGE,"E3")])],"isStart":false}),makeQuery(id+"F5.opExtrude","CAP_FACE",FACE,{"disambiguationData":[OSD([sQuery(id+"F2.wireOp",EDGE,"E4"),sQuery(id+"F2.wireOp",EDGE,"E5"),sQuery(id+"F2.wireOp",EDGE,"E6"),sQuery(id+"F2.wireOp",EDGE,"E7"),sQuery(id+"F2.wireOp",EDGE,"E8"),sQuery(id+"F2.wireOp",EDGE,"E9"),sQuery(id+"F2.wireOp",EDGE,"E10"),sQuery(id+"F2.wireOp",EDGE,"E11")])],"isStart":true})]});
            var sketch = newSketch(context, id + "F8", { "sketchPlane" : qUnion([Q0])});
            skLineSegment(sketch, "E279", {"start": v(168.87, -149.77) * mm, "end": v(227.72, -297.32) * mm});
            skLineSegment(sketch, "E280", {"start": v(227.72, -297.32) * mm, "end": v(168.87, -149.77) * mm});
            skLineSegment(sketch, "E281", {"start": v(168.87, -149.77) * mm, "end": v(168.87, -149.77) * mm});
            skLineSegment(sketch, "E282", {"start": v(227.72, -297.32) * mm, "end": v(306.08, -292.31) * mm});
            skArc(sketch, "E283", {"start": v(306.08, -292.31) * mm, "mid": v(247.9, -211) * mm, "end": v(168.87, -149.77) * mm});
            skSolve(sketch);
        }
        {
            var Q0;
            Q0 = qSketchRegion(id + "F8", true);
            extrude(context, id + "F9", {"entities" : qUnion([Q0]), "operationType" : NewBodyOperationType.REMOVE, "oppositeDirection" : true, "depth" : 662.94 * mm, "offsetDistance" : 25.4 * mm});
        }
    });
